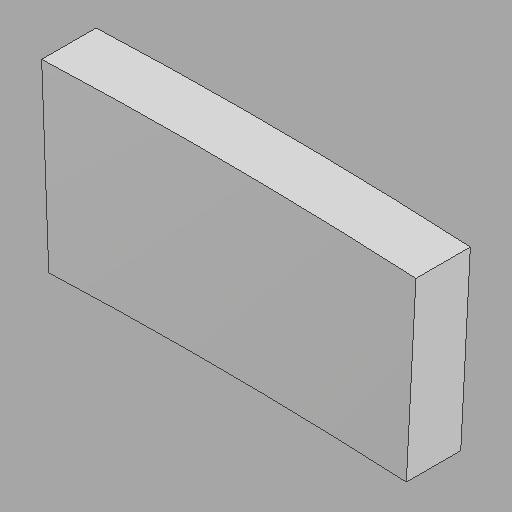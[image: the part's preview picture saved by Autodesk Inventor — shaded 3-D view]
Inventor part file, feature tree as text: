
AUTODESK INVENTOR PART (.ipt)
format: ipt  version: 2022.1 (Build 261234020, 234B)  size: 89,600 bytes
history: imported  units: in
note: dims shown in document units (in); Inventor stores cm internally (conversion verified against a paired STEP export)
features: imported_body x1
ambient origin geometry x8: Origin, YZ Plane, XZ Plane, XY Plane, X Axis, Y Axis, Z Axis, Center Point
bodies: Solid1 (imported_parasolid), Body1 (imported_parasolid)
feature tree (1):
  imported_body  NMx_Import_Brep_tag  [imported B-rep: ~6 faces, bbox_mm=[1047.732119, 514.465119, 152.4]]
